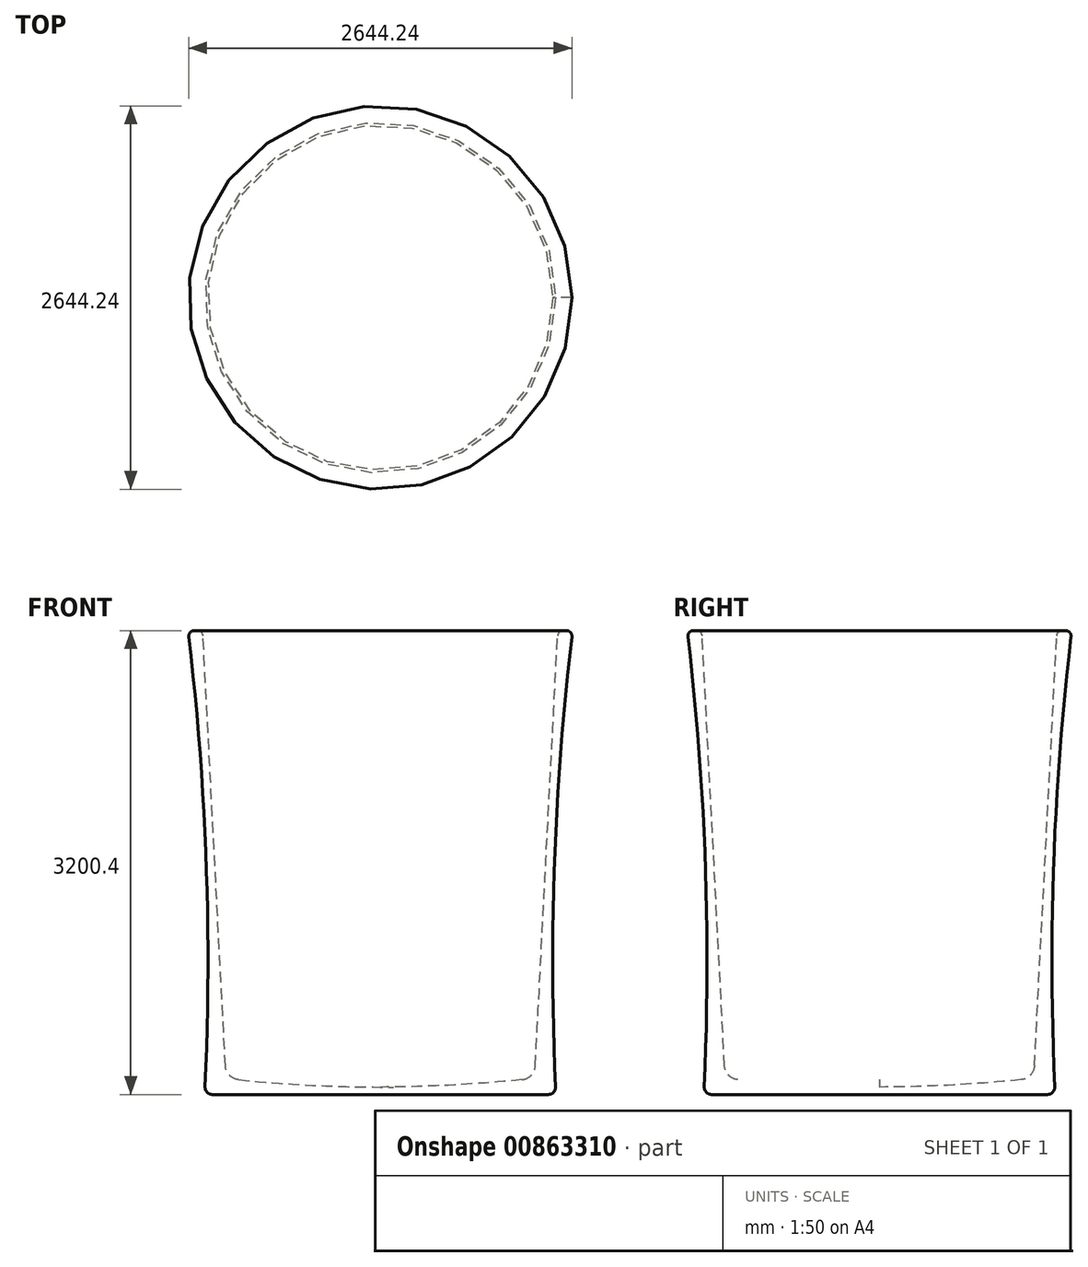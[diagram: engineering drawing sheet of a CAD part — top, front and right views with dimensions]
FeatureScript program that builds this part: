
annotation { "Feature Type Name" : "Feature", "Feature Type Description" : "" }
export const myFeature = defineFeature(function(context is Context, id is Id, definition is map)
    precondition{}
    {
        {
            var Q0;
            Q0=qCreatedBy(makeId("Front.planeOp"),FACE);
            var sketch = newSketch(context, id + "F0", { "sketchPlane" : qUnion([Q0])});
            skPoint(sketch, "E0.visualSharp", {"position": v(-1066.8, 203.2) * mm});
            skLineSegment(sketch, "E1.0", {"start": v(-1334.82, 3251.2) * mm, "end": v(-1312.38, 3251.2) * mm});
            skLineSegment(sketch, "E1.1", {"start": v(-1276.2, 3251.2) * mm, "end": v(-1276.2, 3251.2) * mm});
            skLineSegment(sketch, "E1.2", {"start": v(-1377.74, 3251.2) * mm, "end": v(-1377.74, 3251.2) * mm});
            skLineSegment(sketch, "E1.3", {"start": v(-1120.04, 248.72) * mm, "end": v(-1274.33, 3215.08) * mm});
            skArc(sketch, "E1.4", {"start": v(-1120.04, 248.72) * mm, "mid": v(-1092.13, 183.91) * mm, "end": v(-1028.73, 152.9) * mm});
            skArc(sketch, "E1.5", {"start": v(-1028.73, 152.9) * mm, "mid": v(-540.38, 115.6) * mm, "end": v(-50.8, 101.7) * mm});
            skArc(sketch, "E1.6", {"start": v(-1260.12, 103.9) * mm, "mid": v(-1253.16, 1658.55) * mm, "end": v(-1372.66, 3208.63) * mm});
            skLineSegment(sketch, "E1.8", {"start": v(-50.8, 50.8) * mm, "end": v(-1209.38, 50.8) * mm});
            skLineSegment(sketch, "E1.9", {"start": v(-50.8, 101.7) * mm, "end": v(-50.8, 50.8) * mm});
            skPoint(sketch, "E2.visualSharp", {"position": v(-1262.6, 50.8) * mm});
            skArc(sketch, "E2.filletArc", {"start": v(-1260.12, 103.9) * mm, "mid": v(-1246.1, 66.5) * mm, "end": v(-1209.38, 50.8) * mm});
            skArc(sketch, "E3.filletArc", {"start": v(-1334.82, 3251.2) * mm, "mid": v(-1363.3, 3238.41) * mm, "end": v(-1372.66, 3208.63) * mm});
            skArc(sketch, "E4.filletArc", {"start": v(-1274.33, 3215.08) * mm, "mid": v(-1286.15, 3240.73) * mm, "end": v(-1312.38, 3251.2) * mm});
            skSolve(sketch);
        }
        {
            var Q0;
            Q0=makeQuery(id+"F0.imprint","IMPRINT",FACE,{"disambiguationData":[TD([[makeQuery(id+"F0.imprint","IMPRINT",EDGE,{"derivedFrom":sQuery(id+"F0.wireOp",EDGE,"E1.0")}),-1.0]])]});
            var Q1;
            Q1=sQuery(id+"F0.wireOp",EDGE,"E1.9");
            revolve(context, id + "F1", {"surfaceOperationType" : NewSurfaceOperationType.NEW, "entities" : qUnion([Q0]), "axis" : qUnion([Q1]), "revolveType" : RevolveType.FULL});
        }
    });
